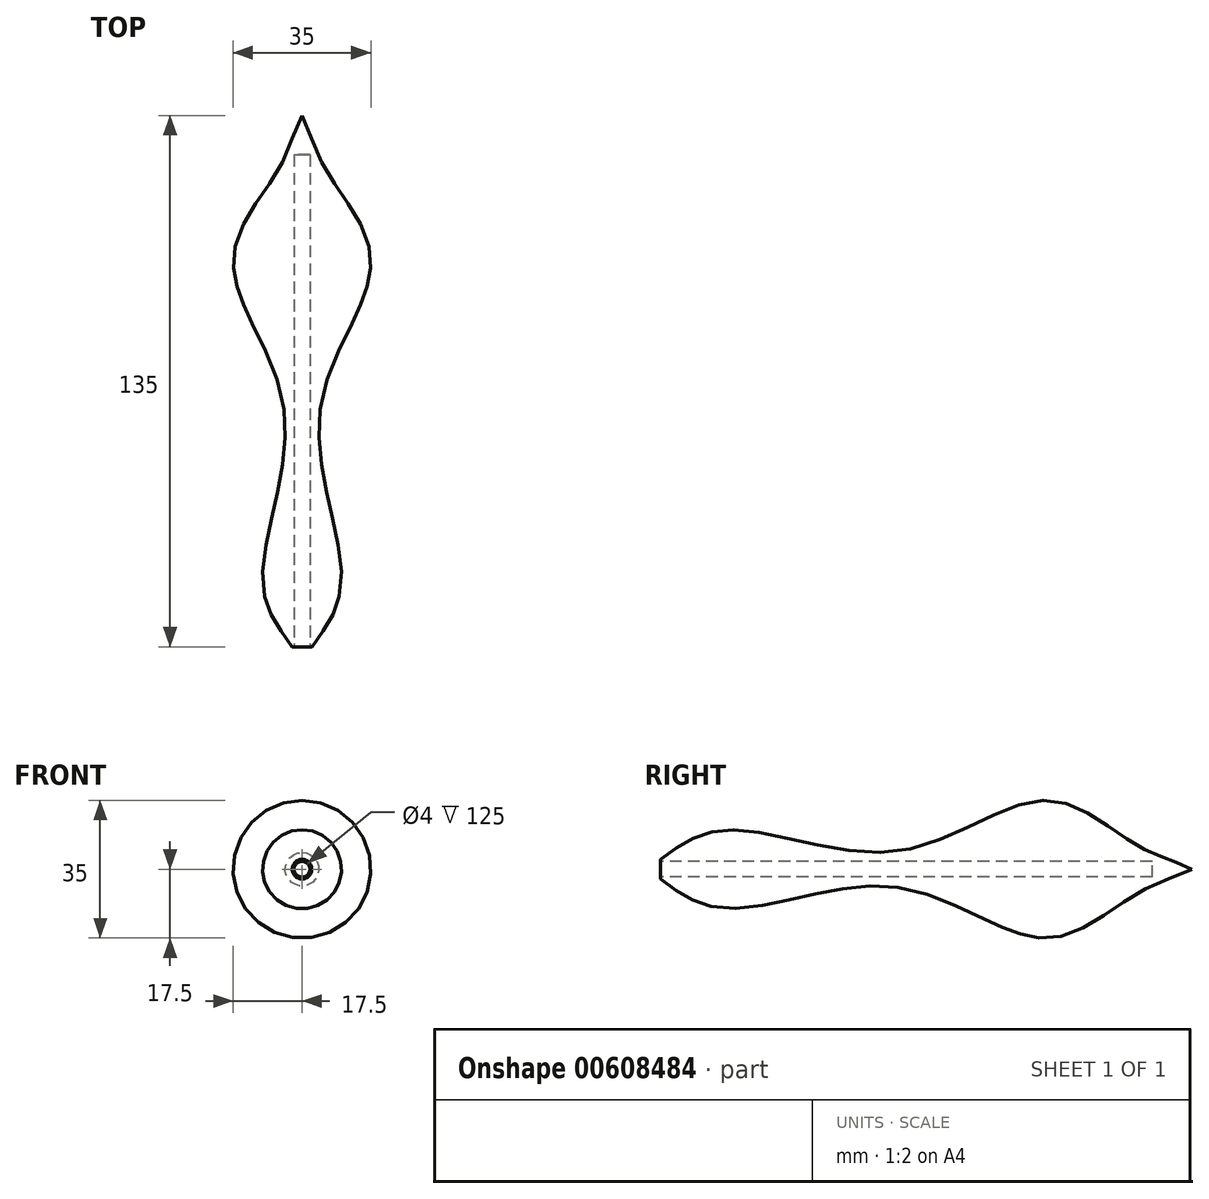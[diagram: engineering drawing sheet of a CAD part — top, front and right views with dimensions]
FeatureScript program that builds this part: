
annotation { "Feature Type Name" : "Feature", "Feature Type Description" : "" }
export const myFeature = defineFeature(function(context is Context, id is Id, definition is map)
    precondition{}
    {
        {
            var Q0;
            Q0=qCreatedBy(makeId("Right.planeOp"),FACE);
            var sketch = newSketch(context, id + "F0", { "sketchPlane" : qUnion([Q0])});
            skLineSegment(sketch, "E0", {"start": v(0, 0) * mm, "end": v(135, 0) * mm});
            skLineSegment(sketch, "E1", {"start": v(0, 0) * mm, "end": v(0, 2.5) * mm});
            skFitSpline(sketch, "E2", {"points": [v(0, 2.5) * mm, v(17.66, 10.04) * mm, v(60.7, 4.64) * mm, v(98, 17.5) * mm, v(121.24, 6.03) * mm, v(135, 0) * mm], "startDerivative": vector(92.59, 70.38) * mm, "endDerivative": vector(90.37, -46.77) * mm});
            skSolve(sketch);
        }
        {
            var Q0;
            {var subQ0=sQuery(id+"F0.wireOp",EDGE,"E1");Q0=makeQuery(id+"F0.imprint","IMPRINT",FACE,{"disambiguationData":[TD([[makeQuery(id+"F0.imprint","IMPRINT",EDGE,{"derivedFrom":subQ0}),-1.0]])]});}
            var Q1;
            Q1=sQuery(id+"F0.wireOp",EDGE,"E0");
            revolve(context, id + "F1", {"entities" : qUnion([Q0]), "axis" : qUnion([Q1]), "revolveType" : RevolveType.FULL});
        }
        {
            var Q0;
            Q0=qCreatedBy(makeId("Front.planeOp"),FACE);
            var sketch = newSketch(context, id + "F2", { "sketchPlane" : qUnion([Q0])});
            skCircle(sketch, "E3", {"center": v(0, 0) * mm, "radius": 2 * mm});
            skSolve(sketch);
        }
        {
            var Q0;
            Q0 = qSketchRegion(id + "F2", true);
            extrude(context, id + "F3", {"entities" : qUnion([Q0]), "operationType" : NewBodyOperationType.REMOVE, "oppositeDirection" : true, "depth" : 125 * mm, "offsetDistance" : 25 * mm});
        }
    });
